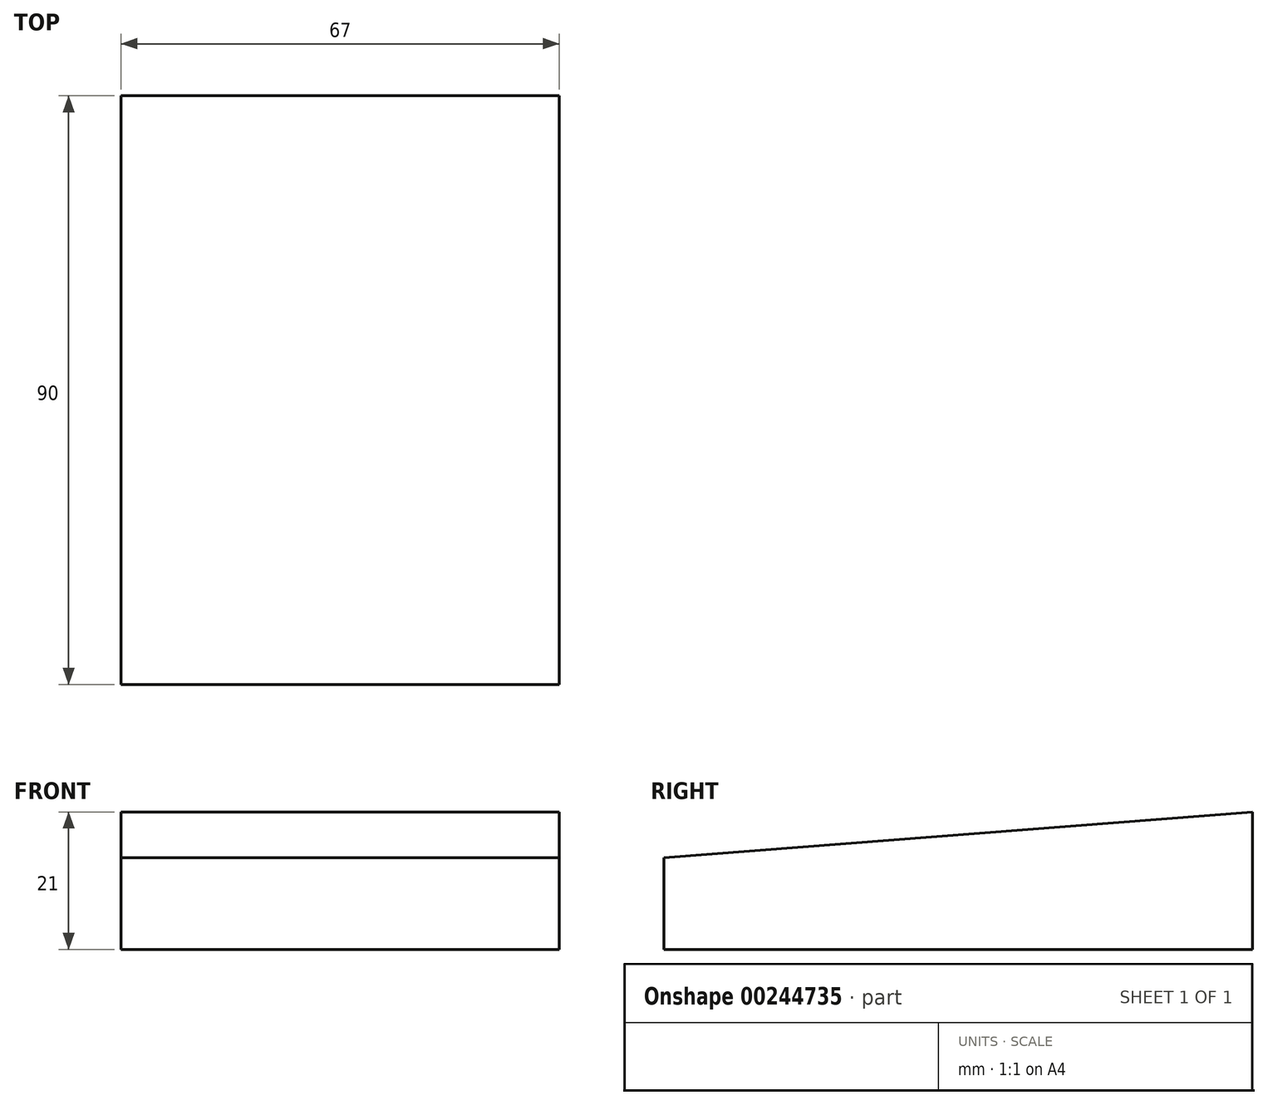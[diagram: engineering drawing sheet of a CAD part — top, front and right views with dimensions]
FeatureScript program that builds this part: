
annotation { "Feature Type Name" : "Feature", "Feature Type Description" : "" }
export const myFeature = defineFeature(function(context is Context, id is Id, definition is map)
    precondition{}
    {
        {
            var Q0;
            Q0=qCreatedBy(makeId("Top.planeOp"),FACE);
            var sketch = newSketch(context, id + "F0", { "sketchPlane" : qUnion([Q0])});
            skLineSegment(sketch, "E0.bottom", {"start": v(-33.5, 45) * mm, "end": v(33.5, 45) * mm});
            skLineSegment(sketch, "E0.top", {"start": v(-33.5, -45) * mm, "end": v(33.5, -45) * mm});
            skLineSegment(sketch, "E0.left", {"start": v(-33.5, 45) * mm, "end": v(-33.5, -45) * mm});
            skLineSegment(sketch, "E0.right", {"start": v(33.5, 45) * mm, "end": v(33.5, -45) * mm});
            skPoint(sketch, "E0.middle", {"position": v(0, 0) * mm});
            skSolve(sketch);
        }
        {
            var Q0;
            Q0=makeQuery(id+"F0.imprint","IMPRINT",FACE,{"disambiguationData":[TD([[makeQuery(id+"F0.imprint","IMPRINT",EDGE,{"derivedFrom":sQuery(id+"F0.wireOp",EDGE,"E0.bottom")}),-1.0]])]});
            extrude(context, id + "F1", {"entities" : qUnion([Q0]), "depth" : 21 * mm});
        }
        {
            var Q0;
            Q0=makeQuery(id+"F1.opExtrude","SWEPT_FACE",FACE,{"disambiguationData":[OSD([sQuery(id+"F0.wireOp",EDGE,"E0.left")])]});
            var sketch = newSketch(context, id + "F2", { "sketchPlane" : qUnion([Q0])});
            skLineSegment(sketch, "E1", {"start": v(45, 0) * mm, "end": v(45, 14) * mm});
            skLineSegment(sketch, "E2", {"start": v(-45, 21) * mm, "end": v(45, 14) * mm});
            skSolve(sketch);
        }
        {
            var Q0;
            {var subQ0=sQuery(id+"F2.wireOp",EDGE,"E2");Q0=makeQuery(id+"F2.imprint","IMPRINT",FACE,{"disambiguationData":[TD([[makeQuery(id+"F2.imprint","IMPRINT",EDGE,{"derivedFrom":subQ0}),1.0]])]});}
            extrude(context, id + "F3", {"entities" : qUnion([Q0]), "operationType" : NewBodyOperationType.REMOVE, "endBound" : BoundingType.THROUGH_ALL, "oppositeDirection" : true, "depth" : 25 * mm});
        }
    });
